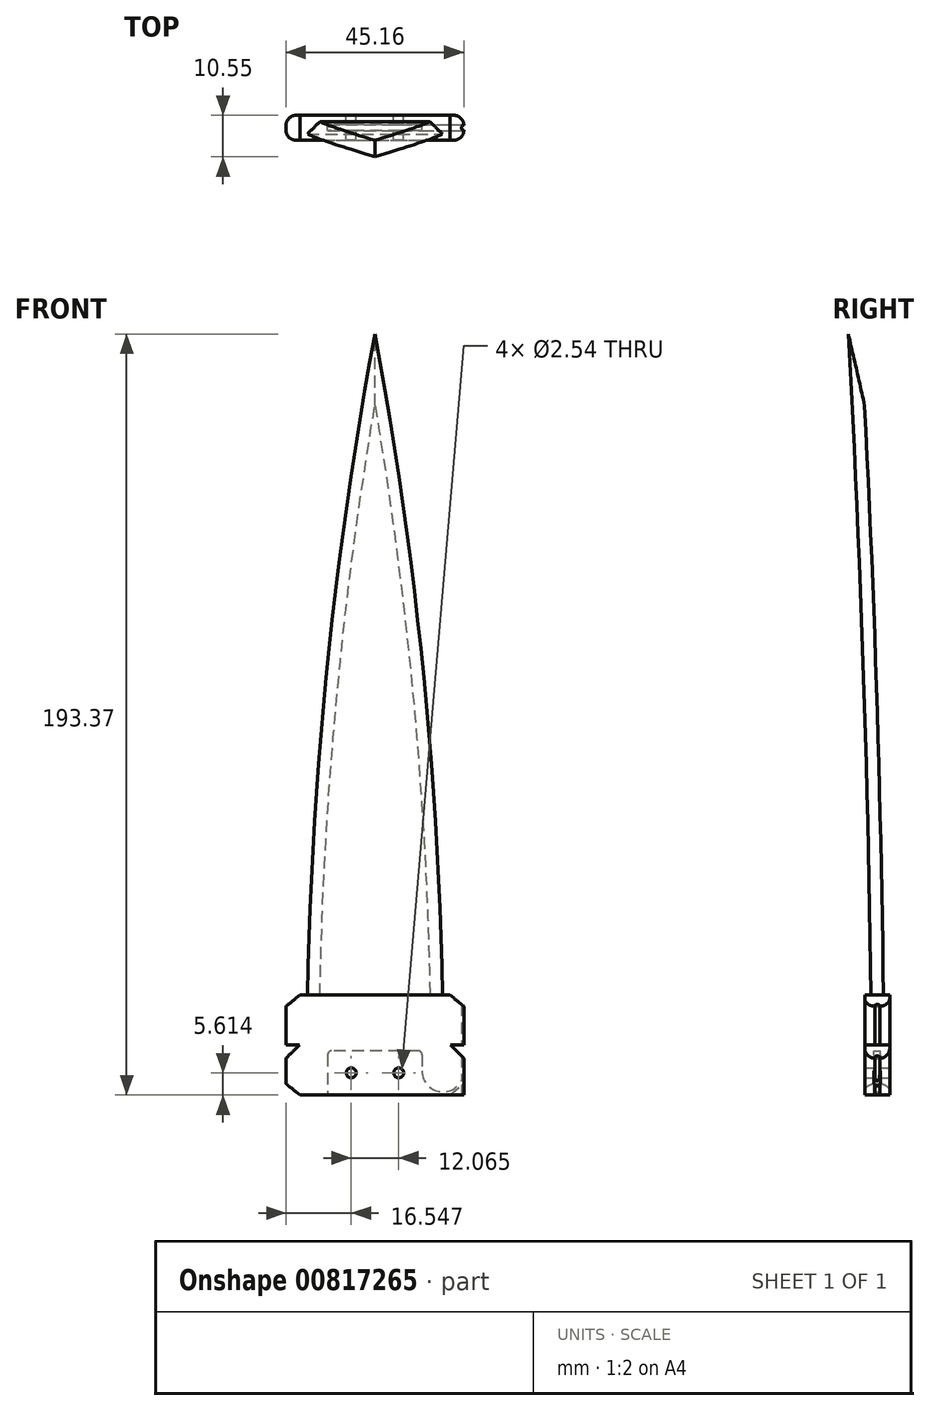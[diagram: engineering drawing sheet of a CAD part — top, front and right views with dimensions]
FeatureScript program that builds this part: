
annotation { "Feature Type Name" : "Feature", "Feature Type Description" : "" }
export const myFeature = defineFeature(function(context is Context, id is Id, definition is map)
    precondition{}
    {
        {
            var Q0;
            Q0=qCreatedBy(makeId("Front.planeOp"),FACE);
            var sketch = newSketch(context, id + "F0", { "sketchPlane" : qUnion([Q0])});
            skLineSegment(sketch, "E0", {"start": v(-19.05, 0) * mm, "end": v(19.05, 0) * mm});
            skArc(sketch, "E1", {"start": v(19.05, 0) * mm, "mid": v(13.42, 89.32) * mm, "end": v(0, 177.8) * mm});
            skPoint(sketch, "E1.endSnap0", {"position": v(0, 0) * mm});
            skArc(sketch, "E2.MirrorCS", {"start": v(-19.05, 0) * mm, "mid": v(-13.42, 89.32) * mm, "end": v(0, 177.8) * mm});
            skLineSegment(sketch, "E3", {"start": v(-19.05, -25.4) * mm, "end": v(0, -25.4) * mm});
            skLineSegment(sketch, "E4", {"start": v(-19.05, 0) * mm, "end": v(-22.58, -2.85) * mm});
            skLineSegment(sketch, "E5", {"start": v(-22.58, -2.85) * mm, "end": v(-22.58, -12.7) * mm});
            skPoint(sketch, "E6.orphan", {"position": v(-19.05, -25.4) * mm});
            skLineSegment(sketch, "E7.MirrorCS", {"start": v(19.05, 0) * mm, "end": v(22.58, -2.85) * mm});
            skLineSegment(sketch, "E8.MirrorCS", {"start": v(22.58, -2.85) * mm, "end": v(22.58, -12.7) * mm});
            skLineSegment(sketch, "E9.MirrorCS", {"start": v(-19.05, -25.4) * mm, "end": v(-22.58, -22.55) * mm});
            skLineSegment(sketch, "E10.MirrorCS", {"start": v(19.05, -25.4) * mm, "end": v(22.58, -22.55) * mm});
            skLineSegment(sketch, "E11.trimOffspring", {"start": v(-22.58, -16.07) * mm, "end": v(-22.58, -22.55) * mm});
            skLineSegment(sketch, "E12", {"start": v(-19.22, -12.7) * mm, "end": v(-22.58, -16.07) * mm});
            skLineSegment(sketch, "E13", {"start": v(-19.22, -12.7) * mm, "end": v(-22.58, -12.7) * mm});
            skLineSegment(sketch, "E14.MirrorCS", {"start": v(19.22, -12.7) * mm, "end": v(22.58, -12.7) * mm});
            skLineSegment(sketch, "E15.MirrorCS", {"start": v(19.22, -12.7) * mm, "end": v(22.58, -16.07) * mm});
            skLineSegment(sketch, "E16.trimOffspring", {"start": v(22.58, -16.07) * mm, "end": v(22.58, -22.55) * mm});
            skLineSegment(sketch, "E17", {"start": v(19.05, -25.4) * mm, "end": v(0, -25.4) * mm});
            skArc(sketch, "E18", {"start": v(-10.99, -14.17) * mm, "mid": v(-11.7, -14.46) * mm, "end": v(-12, -15.17) * mm});
            skCircle(sketch, "E19", {"center": v(-6.03, -19.79) * mm, "radius": 1.27 * mm});
            skLineSegment(sketch, "E20", {"start": v(-12, -15.17) * mm, "end": v(-12, -25.4) * mm});
            skLineSegment(sketch, "E21.MirrorCS", {"start": v(10.99, -14.17) * mm, "end": v(-10.99, -14.17) * mm});
            skLineSegment(sketch, "E22.MirrorCS", {"start": v(12, -15.17) * mm, "end": v(12, -25.4) * mm});
            skArc(sketch, "E23.MirrorC", {"start": v(10.99, -14.17) * mm, "mid": v(11.7, -14.46) * mm, "end": v(12, -15.17) * mm});
            skCircle(sketch, "E24.MirrorC", {"center": v(6.03, -19.79) * mm, "radius": 1.27 * mm});
            skPoint(sketch, "E25.endSnap0", {"position": v(12, -20.29) * mm});
            skPoint(sketch, "E26.endSnap0", {"position": v(22.58, -19.3) * mm});
            skArc(sketch, "E27", {"start": v(12, -19.3) * mm, "mid": v(17.29, -24.6) * mm, "end": v(22.58, -19.3) * mm});
            skPoint(sketch, "E28.start.orphan", {"position": v(-22.58, -25.4) * mm});
            skLineSegment(sketch, "E29", {"start": v(22.58, -22.55) * mm, "end": v(22.58, -25.4) * mm});
            skLineSegment(sketch, "E30", {"start": v(19.05, -25.4) * mm, "end": v(22.58, -25.4) * mm});
            skSolve(sketch);
        }
        {
            var Q0;
            Q0=qCreatedBy(makeId("Right.planeOp"),FACE);
            var sketch = newSketch(context, id + "F1", { "sketchPlane" : qUnion([Q0])});
            skLineSegment(sketch, "E31", {"start": v(0, 0) * mm, "end": v(0, 177.8) * mm});
            skLineSegment(sketch, "E32", {"start": v(0, 177.8) * mm, "end": v(-6.35, 177.8) * mm});
            skArc(sketch, "E33", {"start": v(0, 0) * mm, "mid": v(-2.14, 88.94) * mm, "end": v(-6.35, 177.8) * mm});
            skLineSegment(sketch, "E34", {"start": v(0, 0) * mm, "end": v(-3.18, 0) * mm});
            skLineSegment(sketch, "E35", {"start": v(-6.35, 177.8) * mm, "end": v(-9.53, 177.8) * mm});
            skArc(sketch, "E36.0", {"start": v(-3.17, -0.04) * mm, "mid": v(-5.31, 88.82) * mm, "end": v(-9.52, 177.61) * mm});
            skArc(sketch, "E37.extension", {"start": v(-9.52, 177.61) * mm, "mid": v(-9.53, 177.7) * mm, "end": v(-9.53, 177.8) * mm});
            skPoint(sketch, "E38.orphan", {"position": v(-9.52, 102.63) * mm});
            skLineSegment(sketch, "E39", {"start": v(-9.53, 177.8) * mm, "end": v(-15.88, 177.8) * mm});
            skLineSegment(sketch, "E40", {"start": v(-15.88, 177.8) * mm, "end": v(-15.88, 0.04) * mm});
            skLineSegment(sketch, "E41", {"start": v(-3.17, -0.04) * mm, "end": v(-3.13, -3.25) * mm});
            skLineSegment(sketch, "E42", {"start": v(-3.13, -3.25) * mm, "end": v(-15.87, -3.22) * mm});
            skLineSegment(sketch, "E43", {"start": v(-15.88, -3.22) * mm, "end": v(-15.88, 0.04) * mm});
            skSolve(sketch);
        }
        {
            var Q0;
            Q0=makeQuery(id+"F0.imprint","IMPRINT",FACE,{"disambiguationData":[TD([[makeQuery(id+"F0.imprint","IMPRINT",EDGE,{"derivedFrom":sQuery(id+"F0.wireOp",EDGE,"E0")}),1.0]])]});
            extrude(context, id + "F2", {"entities" : qUnion([Q0]), "depth" : 12.7 * mm, "offsetDistance" : 25.4 * mm});
        }
        {
            var Q0;
            Q0=makeQuery(id+"F1.imprint","IMPRINT",FACE,{"disambiguationData":[TD([[makeQuery(id+"F1.imprint","IMPRINT",EDGE,{"derivedFrom":sQuery(id+"F1.wireOp",EDGE,"E31")}),1.0]])]});
            extrude(context, id + "F3", {"entities" : qUnion([Q0]), "operationType" : NewBodyOperationType.REMOVE, "endBound" : BoundingType.THROUGH_ALL, "depth" : 25.4 * mm, "offsetDistance" : 25.4 * mm, "hasSecondDirection" : true, "secondDirectionBound" : SecondDirectionBoundingType.THROUGH_ALL, "secondDirectionOppositeDirection" : true, "secondDirectionDepth" : 25.4 * mm});
        }
        {
            var Q0;
            {var subQ2=sQuery(id+"F1.wireOp",EDGE,"E37.extension");Q0=makeQuery(id+"F1.imprint","IMPRINT",FACE,{"disambiguationData":[TD([[makeQuery(id+"F1.imprint","IMPRINT",EDGE,{"derivedFrom":subQ2}),1.0]])]});}
            extrude(context, id + "F4", {"entities" : qUnion([Q0]), "operationType" : NewBodyOperationType.REMOVE, "endBound" : BoundingType.THROUGH_ALL, "depth" : 25.4 * mm, "offsetDistance" : 25.4 * mm, "hasSecondDirection" : true, "secondDirectionBound" : SecondDirectionBoundingType.THROUGH_ALL, "secondDirectionOppositeDirection" : true, "secondDirectionDepth" : 25.4 * mm});
        }
        {
            var Q0;
            Q0=makeQuery(id+"F3.boolean.opBoolean","INTERSECT",EDGE,{"derivedFrom":[makeQuery(id+"F2.opExtrude","SWEPT_FACE",FACE,{"disambiguationData":[OSD([sQuery(id+"F0.wireOp",EDGE,"E1")])]}),makeQuery(id+"F3.opExtrude","SWEPT_FACE",FACE,{"disambiguationData":[OSD([sQuery(id+"F1.wireOp",EDGE,"E33")])]})]});
            chamfer(context, id + "F5", {"entities" : qUnion([Q0]), "width" : 5.08 * mm, "tangentPropagation" : true});
        }
        {
            var Q0;
            Q0=makeQuery(id+"F3.boolean.opBoolean","INTERSECT",EDGE,{"derivedFrom":[makeQuery(id+"F2.opExtrude","SWEPT_FACE",FACE,{"disambiguationData":[OSD([sQuery(id+"F0.wireOp",EDGE,"E2.MirrorCS")])]}),makeQuery(id+"F3.opExtrude","SWEPT_FACE",FACE,{"disambiguationData":[OSD([sQuery(id+"F1.wireOp",EDGE,"E33")])]})]});
            chamfer(context, id + "F6", {"entities" : qUnion([Q0]), "width" : 5.08 * mm, "tangentPropagation" : true});
        }
        {
            var Q0;
            Q0=makeQuery(id+"F0.imprint","IMPRINT",FACE,{"disambiguationData":[TD([[makeQuery(id+"F0.imprint","IMPRINT",EDGE,{"derivedFrom":sQuery(id+"F0.wireOp",EDGE,"E0")}),-1.0]])]});
            var Q1;
            Q1=makeQuery(id+"F0.imprint","IMPRINT",FACE,{"disambiguationData":[TD([[makeQuery(id+"F0.imprint","IMPRINT",EDGE,{"derivedFrom":sQuery(id+"F0.wireOp",EDGE,"E18")}),1.0]])]});
            var Q2;
            {var subQ1=sQuery(id+"F0.wireOp",EDGE,"E10.MirrorCS");Q2=makeQuery(id+"F0.imprint","IMPRINT",FACE,{"disambiguationData":[TD([[makeQuery(id+"F0.imprint","IMPRINT",EDGE,{"derivedFrom":subQ1}),1.0]])]});}
            var Q3;
            Q3=makeQuery(id+"F0.imprint","IMPRINT",FACE,{"disambiguationData":[TD([[makeQuery(id+"F0.imprint","IMPRINT",EDGE,{"derivedFrom":sQuery(id+"F0.wireOp",EDGE,"E10.MirrorCS")}),-1.0]])]});
            extrude(context, id + "F7", {"entities" : qUnion([Q0, Q1, Q2, Q3]), "operationType" : NewBodyOperationType.ADD, "depth" : 4.76 * mm, "offsetDistance" : 25.4 * mm, "hasSecondDirection" : true, "secondDirectionOppositeDirection" : true, "secondDirectionDepth" : 1.59 * mm});
        }
        {
            var Q0;
            Q0=makeQuery(id+"F7.opExtrude","CAP_EDGE",EDGE,{"disambiguationData":[OSD([sQuery(id+"F0.wireOp",EDGE,"E8.MirrorCS")])],"isStart":true});
            var Q1;
            Q1=makeQuery(id+"F7.opExtrude","CAP_EDGE",EDGE,{"disambiguationData":[OSD([sQuery(id+"F0.wireOp",EDGE,"E8.MirrorCS")])],"isStart":false});
            var Q2;
            Q2=makeQuery(id+"F7.opExtrude","CAP_EDGE",EDGE,{"disambiguationData":[OSD([sQuery(id+"F0.wireOp",EDGE,"E16.trimOffspring")])],"isStart":true});
            var Q3;
            Q3=makeQuery(id+"F7.opExtrude","CAP_EDGE",EDGE,{"disambiguationData":[OSD([sQuery(id+"F0.wireOp",EDGE,"E16.trimOffspring")])],"isStart":false});
            var Q4;
            Q4=makeQuery(id+"F7.opExtrude","CAP_EDGE",EDGE,{"disambiguationData":[OSD([sQuery(id+"F0.wireOp",EDGE,"E5")])],"isStart":true});
            var Q5;
            Q5=makeQuery(id+"F7.opExtrude","CAP_EDGE",EDGE,{"disambiguationData":[OSD([sQuery(id+"F0.wireOp",EDGE,"E5")])],"isStart":false});
            var Q6;
            Q6=makeQuery(id+"F7.opExtrude","CAP_EDGE",EDGE,{"disambiguationData":[OSD([sQuery(id+"F0.wireOp",EDGE,"E11.trimOffspring")])],"isStart":true});
            var Q7;
            Q7=makeQuery(id+"F7.opExtrude","CAP_EDGE",EDGE,{"disambiguationData":[OSD([sQuery(id+"F0.wireOp",EDGE,"E11.trimOffspring")])],"isStart":false});
            fillet(context, id + "F8", {"entities" : qUnion([Q0, Q1, Q2, Q3, Q4, Q5, Q6, Q7]), "radius" : 2.54 * mm, "tangentPropagation" : true, "allowEdgeOverflow" : false});
        }
        {
            var Q0;
            Q0=makeQuery(id+"F0.imprint","IMPRINT",FACE,{"disambiguationData":[TD([[makeQuery(id+"F0.imprint","IMPRINT",EDGE,{"derivedFrom":sQuery(id+"F0.wireOp",EDGE,"E18")}),1.0]])]});
            var Q1;
            {var subQ1=sQuery(id+"F0.wireOp",EDGE,"E10.MirrorCS");Q1=makeQuery(id+"F0.imprint","IMPRINT",FACE,{"disambiguationData":[TD([[makeQuery(id+"F0.imprint","IMPRINT",EDGE,{"derivedFrom":subQ1}),1.0]])]});}
            extrude(context, id + "F9", {"entities" : qUnion([Q0, Q1]), "operationType" : NewBodyOperationType.REMOVE, "depth" : 2.38 * mm, "offsetDistance" : 25.4 * mm, "hasSecondDirection" : true, "secondDirectionOppositeDirection" : false, "secondDirectionDepth" : 0.8 * mm});
        }
        {
            var Q0;
            Q0=makeQuery(id+"F7.opExtrude","SWEPT_FACE",FACE,{"disambiguationData":[OSD([sQuery(id+"F0.wireOp",EDGE,"E14.MirrorCS")])]});
            var sketch = newSketch(context, id + "F10", { "sketchPlane" : qUnion([Q0])});
            skLineSegment(sketch, "E44", {"start": v(22.58, 0.95) * mm, "end": v(22.58, 2.22) * mm});
            skArc(sketch, "E45", {"start": v(22.58, 2.22) * mm, "mid": v(21.95, 1.59) * mm, "end": v(22.58, 0.95) * mm});
            skSolve(sketch);
        }
        {
            var Q0;
            Q0=makeQuery(id+"F10.imprint","IMPRINT",FACE,{"disambiguationData":[TD([[makeQuery(id+"F10.imprint","IMPRINT",EDGE,{"derivedFrom":sQuery(id+"F10.wireOp",EDGE,"E44")}),-1.0]])]});
            extrude(context, id + "F11", {"entities" : qUnion([Q0]), "operationType" : NewBodyOperationType.REMOVE, "endBound" : BoundingType.THROUGH_ALL, "oppositeDirection" : true, "depth" : 25.4 * mm, "offsetDistance" : 25.4 * mm, "hasSecondDirection" : true, "secondDirectionBound" : SecondDirectionBoundingType.THROUGH_ALL, "secondDirectionOppositeDirection" : false, "secondDirectionDepth" : 25.4 * mm});
        }
    });
